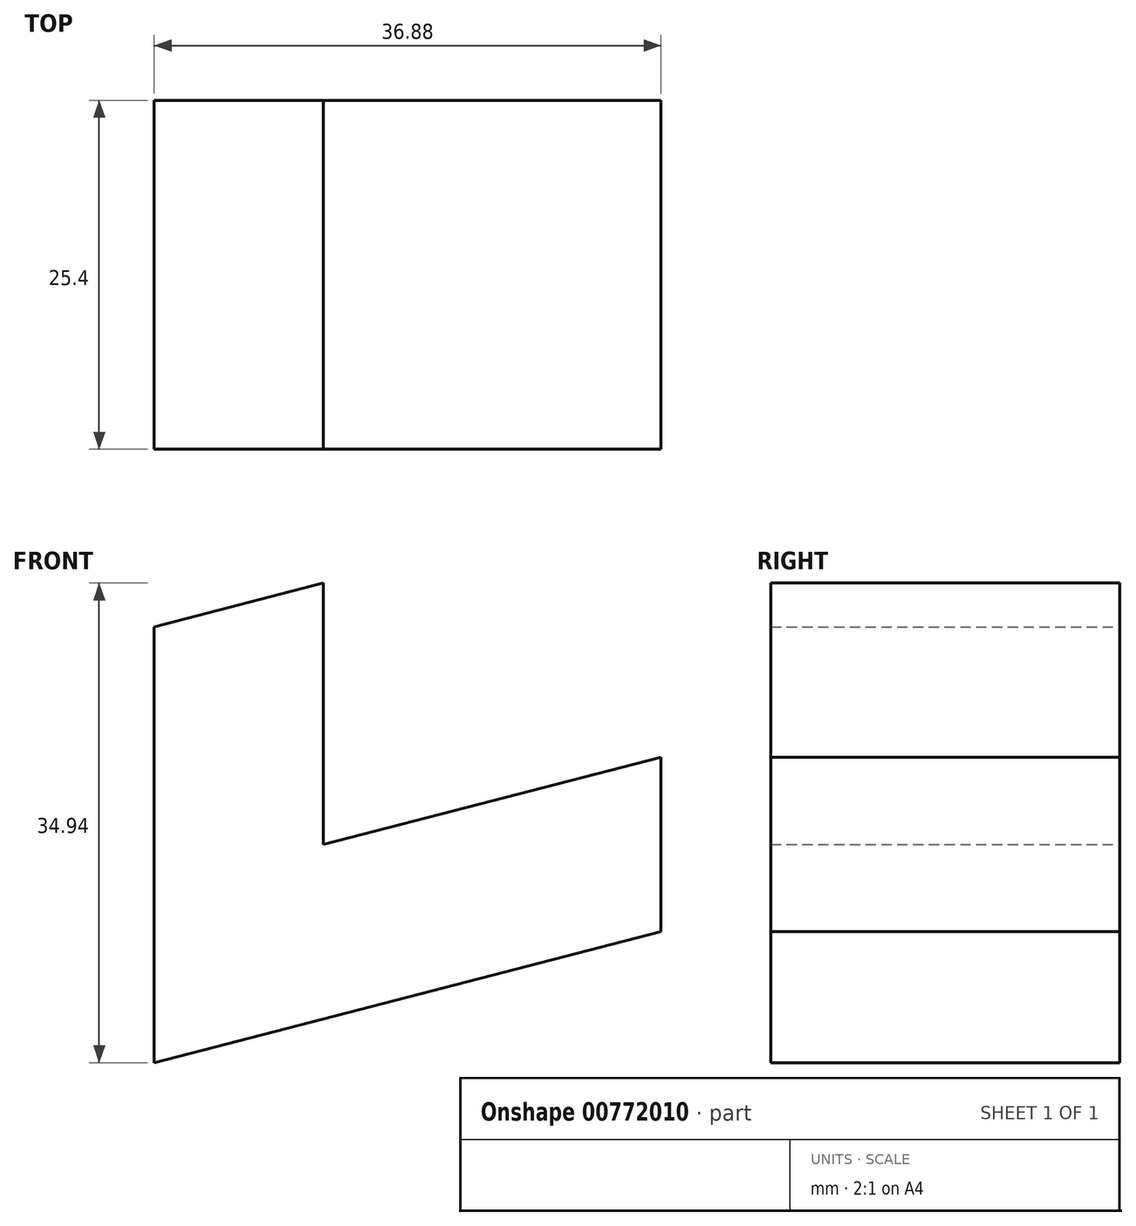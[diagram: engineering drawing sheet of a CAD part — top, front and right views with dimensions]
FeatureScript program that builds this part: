
annotation { "Feature Type Name" : "Feature", "Feature Type Description" : "" }
export const myFeature = defineFeature(function(context is Context, id is Id, definition is map)
    precondition{}
    {
        {
            var Q0;
            Q0=qCreatedBy(makeId("Front.planeOp"),FACE);
            var sketch = newSketch(context, id + "F0", { "sketchPlane" : qUnion([Q0])});
            skLineSegment(sketch, "E0", {"start": v(0, 0) * mm, "end": v(-36.88, -9.56) * mm});
            skLineSegment(sketch, "E1", {"start": v(-36.88, -9.56) * mm, "end": v(-36.88, 22.2) * mm});
            skLineSegment(sketch, "E2", {"start": v(0, 0) * mm, "end": v(0, 12.7) * mm});
            skLineSegment(sketch, "E3", {"start": v(0, 12.7) * mm, "end": v(-24.59, 6.33) * mm});
            skLineSegment(sketch, "E4", {"start": v(-24.59, 6.33) * mm, "end": v(-24.59, 25.38) * mm});
            skLineSegment(sketch, "E5", {"start": v(-24.59, 25.38) * mm, "end": v(-36.88, 22.2) * mm});
            skSolve(sketch);
        }
        {
            var Q0;
            Q0 = qSketchRegion(id + "F0", true);
            extrude(context, id + "F1", {"entities" : qUnion([Q0]), "depth" : 25.4 * mm, "offsetDistance" : 25.4 * mm});
        }
    });
